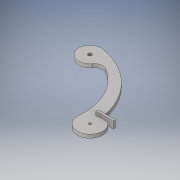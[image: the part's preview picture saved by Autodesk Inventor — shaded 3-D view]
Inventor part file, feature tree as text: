
AUTODESK INVENTOR PART (.ipt)
format: ipt  version: 2016 (Build 200138000, 138)  size: 197,120 bytes
history: native  units: in
note: dims shown in document units (in); Inventor stores cm internally (conversion verified against a paired STEP export)
features: extrude x10, sketch x10, fillet x3, mirror x1
ambient origin geometry x8: Origin, YZ Plane, XZ Plane, XY Plane, X Axis, Y Axis, Z Axis, Center Point
bodies: Solid1 (feature_tree)
feature tree (24):
  extrude  "Extrusion1"  Depth=0.9in
  extrude  "Extrusion2"  Depth=0.125in TaperAngle=0.0deg
  extrude  "Extrusion3"  Depth=0.3125in TaperAngle=0.0deg
  extrude  "Extrusion6"  Depth=0.45in TaperAngle=0.0deg
  extrude  "Extrusion7"  Depth=0.25in TaperAngle=0.0deg
  extrude  "Extrusion8"  Depth=0.25in TaperAngle=0.0deg
  extrude  "Extrusion9"  TaperAngle=135.0deg  [1 undecoded]
  extrude  "Extrusion13"  Depth=0.125in
  fillet  "Fillet3"  Radius=0.1299in
  fillet  "Fillet4"  Radius=0.1299in
  fillet  "Fillet5"  Radius=0.125in
  mirror  "Mirror1"
  extrude  "Extrusion14"  Depth=0.3in
  extrude  "Extrusion15"  Depth=0.125in TaperAngle=0.0deg
  sketch  "Sketch1"  dims[d0=0.9in d1=0.75in]
  sketch  "Sketch2"  dims[d2=0.25in d3=0.0in d4=0.125in d5=0.0in]
  sketch  "Sketch3"  dims[d6=0.0866in d7=0.3125in d8=0.0in]
  sketch  "Sketch6"  dims[d14=0.25in d15=0.0in d16=0.45in d17=0.0in]
  sketch  "Sketch7"  dims[d18=135.0deg d19=0.25in d20=0.0in]
  sketch  "Sketch8"  dims[d21=112.5deg d22=0.25in d23=0.0in]
  sketch  "Sketch9"  dims[d44=3.0in d45=135.0deg]
  sketch  "Sketch13"  dims[d46=0.8in d47=0.6918in d48=0.1299in d49=0.1299in d50=0.125in d51=0.0in]
  sketch  "Sketch14"  dims[d52=2.0in d53=0.3in]
  sketch  "Sketch15"  dims[d54=2.5in d55=0.125in d56=0.0in d57=1.0625in d58=0.0in]
note: 1 required parameter value undecoded (feature->parameter linkage not recoverable at this tier; creation-order binding heuristic only, values carry confidence <= 0.55)
